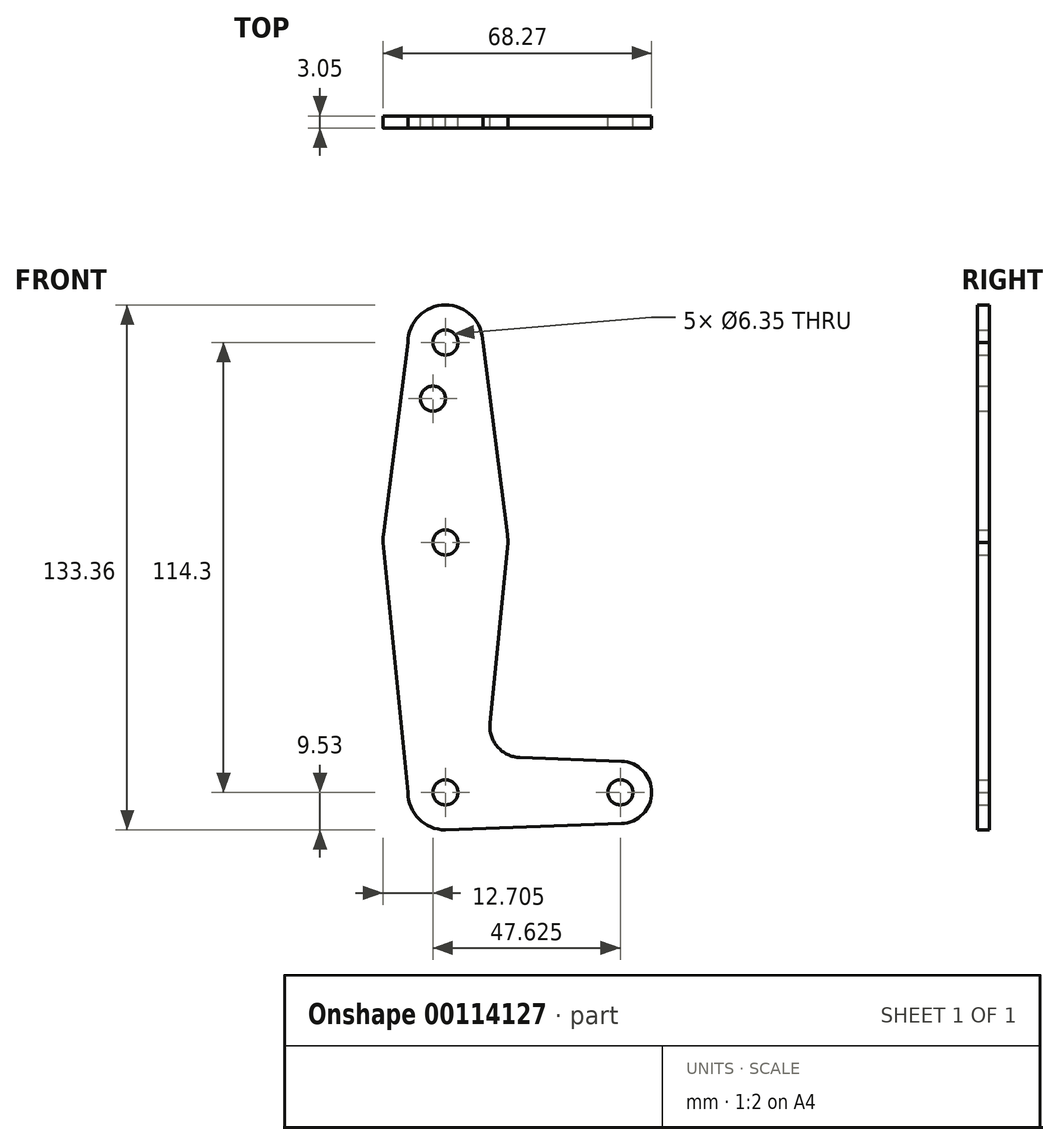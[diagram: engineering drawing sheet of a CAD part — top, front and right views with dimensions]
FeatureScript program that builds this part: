
annotation { "Feature Type Name" : "Feature", "Feature Type Description" : "" }
export const myFeature = defineFeature(function(context is Context, id is Id, definition is map)
    precondition{}
    {
        {
            var Q0;
            Q0=qCreatedBy(makeId("Front.planeOp"),FACE);
            var sketch = newSketch(context, id + "F0", { "sketchPlane" : qUnion([Q0])});
            skCircle(sketch, "E0", {"center": v(0, 0) * mm, "radius": 9.53 * mm});
            skCircle(sketch, "E1", {"center": v(0, 63.5) * mm, "radius": 15.88 * mm});
            skCircle(sketch, "E2", {"center": v(0, 114.3) * mm, "radius": 9.53 * mm});
            skCircle(sketch, "E3", {"center": v(44.45, 0) * mm, "radius": 7.94 * mm});
            skLineSegment(sketch, "E4", {"start": v(0, 114.3) * mm, "end": v(0, 0) * mm, "construction": true});
            skLineSegment(sketch, "E5", {"start": v(0, 0) * mm, "end": v(44.45, 0) * mm, "construction": true});
            skLineSegment(sketch, "E6", {"start": v(-9.52, 114.3) * mm, "end": v(-15.75, 65.5) * mm});
            skLineSegment(sketch, "E7", {"start": v(9.52, 114.3) * mm, "end": v(15.75, 65.5) * mm});
            skLineSegment(sketch, "E8", {"start": v(15.87, 63.5) * mm, "end": v(11.32, 17.58) * mm});
            skLineSegment(sketch, "E9", {"start": v(-15.88, 63.5) * mm, "end": v(-9.53, 0) * mm});
            skLineSegment(sketch, "E10", {"start": v(0, -9.52) * mm, "end": v(44.73, -7.93) * mm});
            skLineSegment(sketch, "E11", {"start": v(18.94, 8.85) * mm, "end": v(44.73, 7.93) * mm});
            skCircle(sketch, "E12", {"center": v(0, 114.3) * mm, "radius": 3.18 * mm});
            skCircle(sketch, "E13", {"center": v(-3.17, 100.03) * mm, "radius": 3.18 * mm});
            skCircle(sketch, "E14", {"center": v(0, 63.5) * mm, "radius": 3.18 * mm});
            skCircle(sketch, "E15", {"center": v(0, 0) * mm, "radius": 3.18 * mm});
            skCircle(sketch, "E16", {"center": v(44.45, 0) * mm, "radius": 3.18 * mm});
            skArc(sketch, "E17.filletArc", {"start": v(11.32, 17.58) * mm, "mid": v(13.24, 11.57) * mm, "end": v(18.94, 8.85) * mm});
            skSolve(sketch);
        }
        {
            var Q0;
            {var subQ0=sQuery(id+"F0.wireOp",EDGE,"E10");var subQ1=sQuery(id+"F0.wireOp",EDGE,"E0");var subQ2=makeQuery(id+"F0.imprint","INTERSECT",VERTEX,{"disambiguationData":[OD(0.0)],"derivedFrom":[subQ1,subQ0]});Q0=makeQuery(id+"F0.imprint","IMPRINT",FACE,{"disambiguationData":[TD([[makeQuery(id+"F0.imprint","IMPRINT",EDGE,{"disambiguationData":[TD([[subQ2,-1.0]])],"derivedFrom":subQ1}),1.0]])]});}
            var Q1;
            {var subQ0=sQuery(id+"F0.wireOp",EDGE,"E9");var subQ1=sQuery(id+"F0.wireOp",EDGE,"E1");var subQ2=makeQuery(id+"F0.imprint","INTERSECT",VERTEX,{"disambiguationData":[OD(0.0)],"derivedFrom":[subQ1,subQ0]});Q1=makeQuery(id+"F0.imprint","IMPRINT",FACE,{"disambiguationData":[TD([[makeQuery(id+"F0.imprint","IMPRINT",EDGE,{"disambiguationData":[TD([[subQ2,-1.0]])],"derivedFrom":subQ1}),1.0]])]});}
            var Q2;
            {var subQ0=sQuery(id+"F0.wireOp",EDGE,"E8");var subQ1=sQuery(id+"F0.wireOp",EDGE,"E1");var subQ2=makeQuery(id+"F0.imprint","INTERSECT",VERTEX,{"disambiguationData":[OD(0.0)],"derivedFrom":[subQ1,subQ0]});Q2=makeQuery(id+"F0.imprint","IMPRINT",FACE,{"disambiguationData":[TD([[makeQuery(id+"F0.imprint","IMPRINT",EDGE,{"disambiguationData":[TD([[subQ2,1.0]])],"derivedFrom":subQ1}),1.0]])]});}
            var Q3;
            Q3=makeQuery(id+"F0.imprint","IMPRINT",FACE,{"disambiguationData":[TD([[makeQuery(id+"F0.imprint","IMPRINT",EDGE,{"derivedFrom":sQuery(id+"F0.wireOp",EDGE,"E12")}),-1.0]])]});
            var Q4;
            Q4=makeQuery(id+"F0.imprint","IMPRINT",FACE,{"disambiguationData":[TD([[makeQuery(id+"F0.imprint","IMPRINT",EDGE,{"derivedFrom":sQuery(id+"F0.wireOp",EDGE,"E16")}),-1.0]])]});
            var Q5;
            Q5=makeQuery(id+"F0.imprint","IMPRINT",FACE,{"disambiguationData":[TD([[makeQuery(id+"F0.imprint","IMPRINT",EDGE,{"derivedFrom":sQuery(id+"F0.wireOp",EDGE,"E15")}),-1.0]])]});
            var Q6;
            {var subQ1=sQuery(id+"F0.wireOp",EDGE,"E6");Q6=makeQuery(id+"F0.imprint","IMPRINT",FACE,{"disambiguationData":[TD([[makeQuery(id+"F0.imprint","IMPRINT",EDGE,{"derivedFrom":subQ1}),1.0]])]});}
            var Q7;
            Q7=makeQuery(id+"F0.imprint","IMPRINT",FACE,{"disambiguationData":[TD([[makeQuery(id+"F0.imprint","IMPRINT",EDGE,{"derivedFrom":sQuery(id+"F0.wireOp",EDGE,"E14")}),-1.0]])]});
            var Q8;
            {var subQ3=sQuery(id+"F0.wireOp",EDGE,"E11");Q8=makeQuery(id+"F0.imprint","IMPRINT",FACE,{"disambiguationData":[TD([[makeQuery(id+"F0.imprint","IMPRINT",EDGE,{"derivedFrom":subQ3}),-1.0]])]});}
            extrude(context, id + "F1", {"entities" : qUnion([Q0, Q1, Q2, Q3, Q4, Q5, Q6, Q7, Q8]), "depth" : 3.05 * mm});
        }
    });
